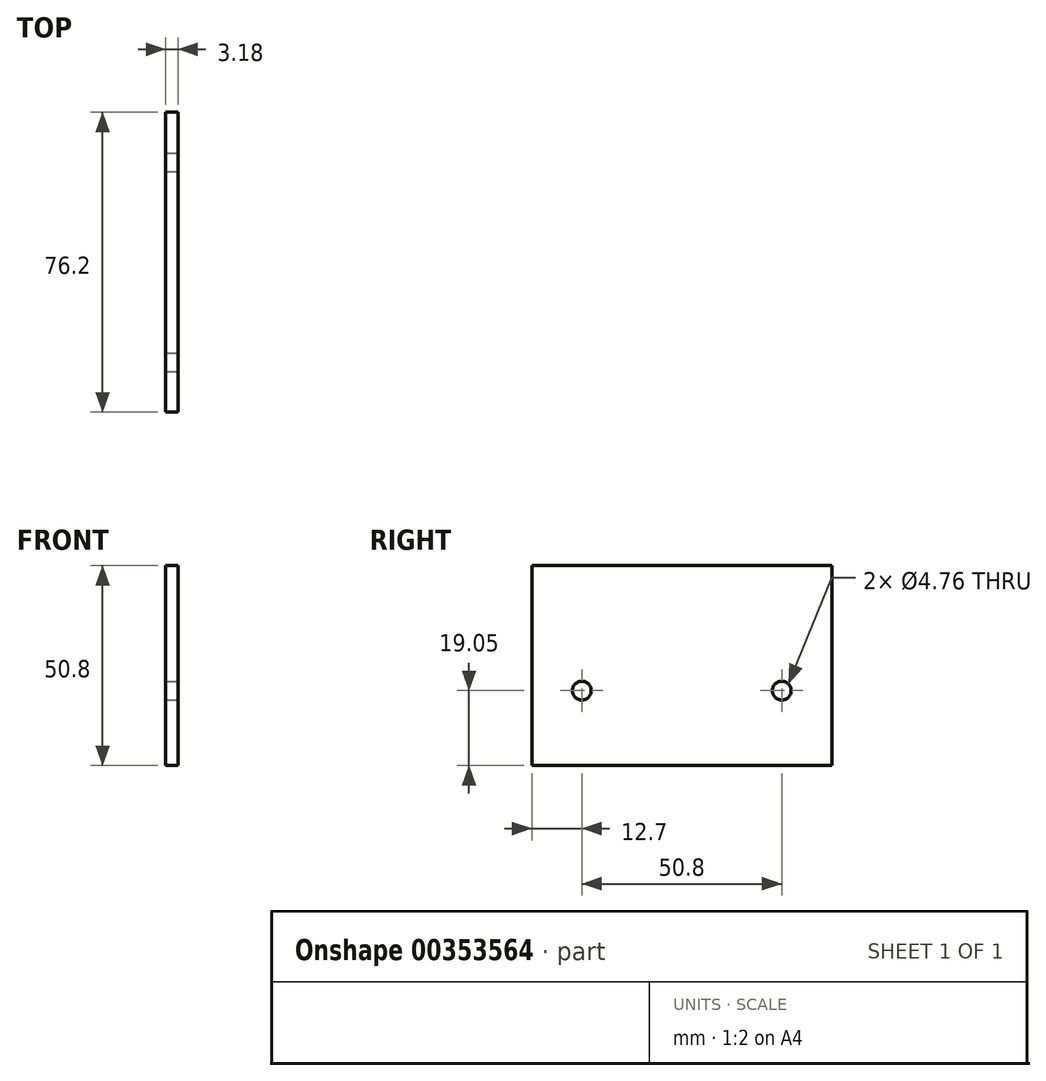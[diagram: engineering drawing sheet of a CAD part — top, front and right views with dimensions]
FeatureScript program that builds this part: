
annotation { "Feature Type Name" : "Feature", "Feature Type Description" : "" }
export const myFeature = defineFeature(function(context is Context, id is Id, definition is map)
    precondition{}
    {
        {
            var Q0;
            Q0=qCreatedBy(makeId("Front.planeOp"),FACE);
            var sketch = newSketch(context, id + "F0", { "sketchPlane" : qUnion([Q0])});
            skLineSegment(sketch, "E0.bottom", {"start": v(1.59, 25.4) * mm, "end": v(-1.59, 25.4) * mm});
            skLineSegment(sketch, "E0.top", {"start": v(1.59, -25.4) * mm, "end": v(-1.59, -25.4) * mm});
            skLineSegment(sketch, "E0.left", {"start": v(1.59, 25.4) * mm, "end": v(1.59, -25.4) * mm});
            skLineSegment(sketch, "E0.right", {"start": v(-1.59, 25.4) * mm, "end": v(-1.59, -25.4) * mm});
            skPoint(sketch, "E0.middle", {"position": v(0, 0) * mm});
            skSolve(sketch);
        }
        {
            var Q0;
            Q0 = qSketchRegion(id + "F0", true);
            extrude(context, id + "F1", {"entities" : qUnion([Q0]), "depth" : 76.2 * mm, "symmetric" : true});
        }
        {
            var Q0;
            Q0=makeQuery(id+"F1.opExtrude","SWEPT_FACE",FACE,{"disambiguationData":[OSD([sQuery(id+"F0.wireOp",EDGE,"E0.left")])]});
            var sketch = newSketch(context, id + "F2", { "sketchPlane" : qUnion([Q0])});
            skCircle(sketch, "E1", {"center": v(25.4, -6.35) * mm, "radius": 2.38 * mm});
            skCircle(sketch, "E2", {"center": v(-25.4, -6.35) * mm, "radius": 2.38 * mm});
            skSolve(sketch);
        }
        {
            var Q0;
            Q0 = qSketchRegion(id + "F2", true);
            extrude(context, id + "F3", {"entities" : qUnion([Q0]), "operationType" : NewBodyOperationType.REMOVE, "oppositeDirection" : true, "depth" : 25.4 * mm});
        }
    });
